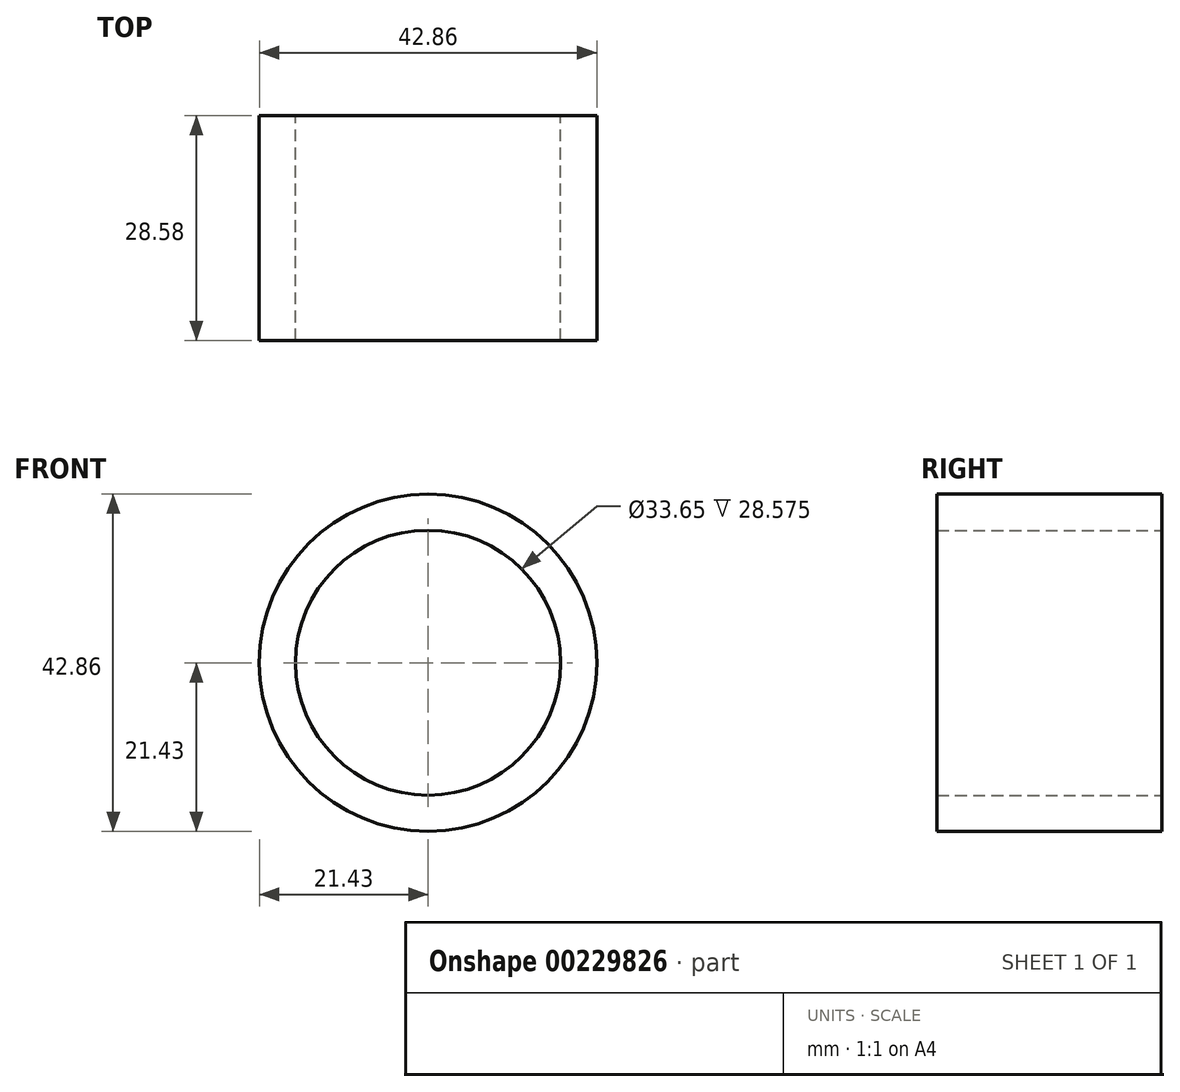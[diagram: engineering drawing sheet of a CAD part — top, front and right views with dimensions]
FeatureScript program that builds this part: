
annotation { "Feature Type Name" : "Feature", "Feature Type Description" : "" }
export const myFeature = defineFeature(function(context is Context, id is Id, definition is map)
    precondition{}
    {
        {
            var Q0;
            Q0=qCreatedBy(makeId("Front.planeOp"),FACE);
            var sketch = newSketch(context, id + "F0", { "sketchPlane" : qUnion([Q0])});
            skCircle(sketch, "E0", {"center": v(0, 0) * mm, "radius": 16.83 * mm});
            skCircle(sketch, "E1", {"center": v(0, 0) * mm, "radius": 21.43 * mm});
            skSolve(sketch);
        }
        {
            var Q0;
            Q0 = qSketchRegion(id + "F0", true);
            extrude(context, id + "F1", {"entities" : qUnion([Q0]), "depth" : 28.57 * mm});
        }
    });
